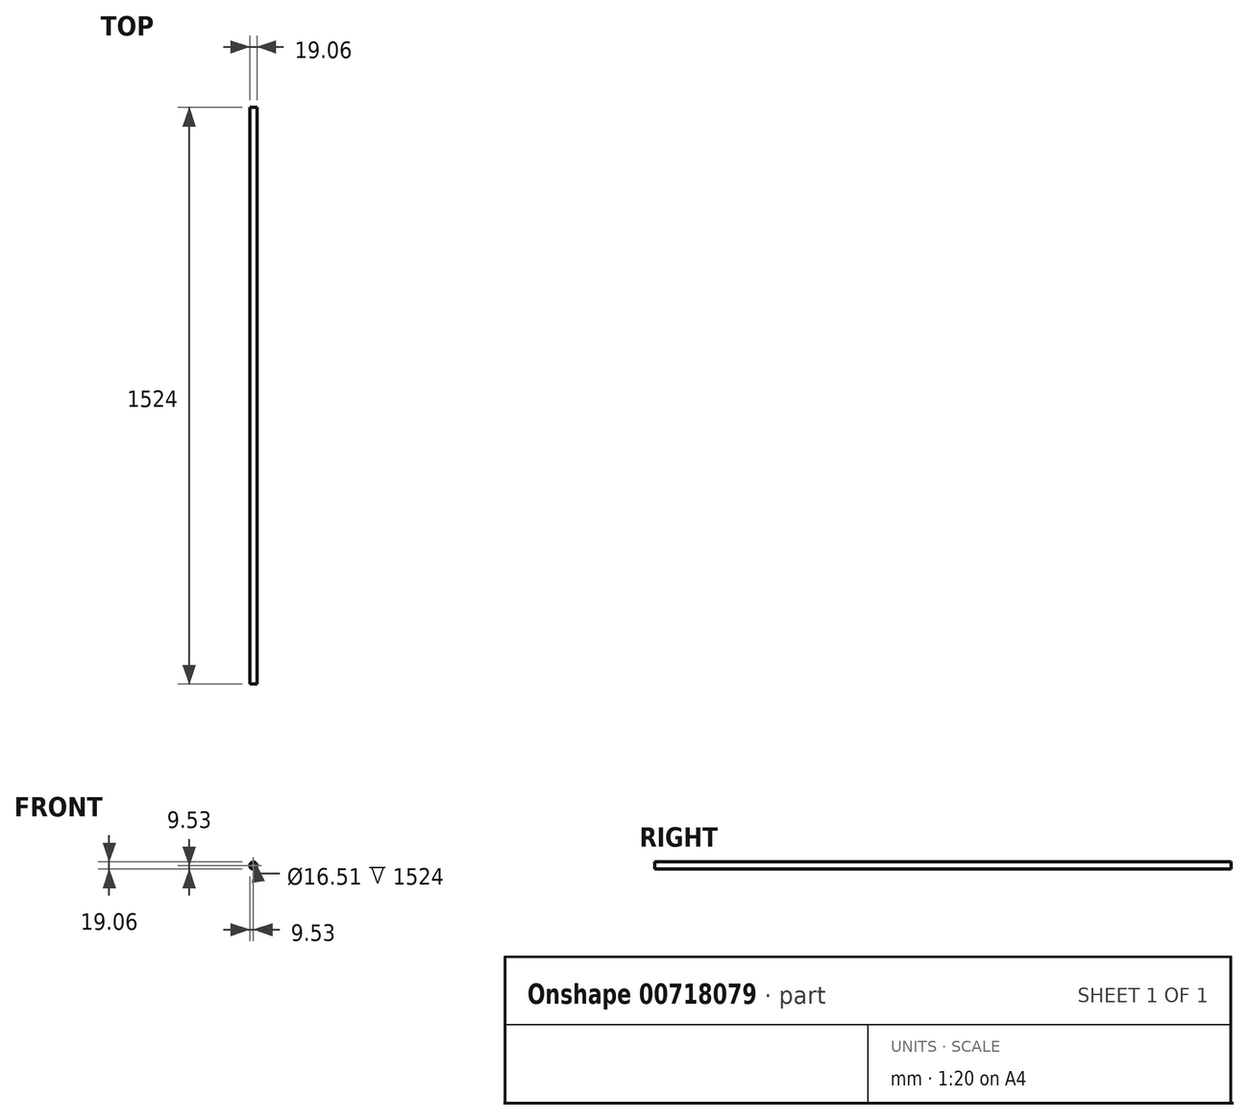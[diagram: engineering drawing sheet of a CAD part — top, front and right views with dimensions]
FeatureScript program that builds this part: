
annotation { "Feature Type Name" : "Feature", "Feature Type Description" : "" }
export const myFeature = defineFeature(function(context is Context, id is Id, definition is map)
    precondition{}
    {
        {
            var Q0;
            Q0=qCreatedBy(makeId("Front.planeOp"),FACE);
            var sketch = newSketch(context, id + "F0", { "sketchPlane" : qUnion([Q0])});
            skCircle(sketch, "E0", {"center": v(0, 0) * mm, "radius": 9.53 * mm});
            skCircle(sketch, "E1", {"center": v(0, 0) * mm, "radius": 8.26 * mm});
            skSolve(sketch);
        }
        {
            var Q0;
            Q0 = qSketchRegion(id + "F0", true);
            extrude(context, id + "F1", {"entities" : qUnion([Q0]), "depth" : 1524 * mm, "offsetDistance" : 25.4 * mm});
        }
    });
